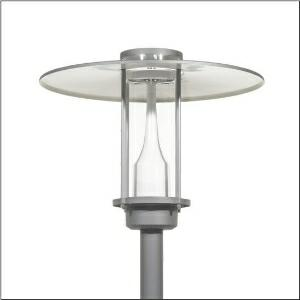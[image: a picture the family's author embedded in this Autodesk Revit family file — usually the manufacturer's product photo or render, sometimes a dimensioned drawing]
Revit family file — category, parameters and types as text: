
# Revit family: city-light_plus_iq___p1_0a_5xa5275bf14hp_a9e6
name_source: partatom
category: Lighting Fixtures
units: mm (PartAtom-declared; Revit-internal decimal feet)

## family parameters
Cut with Voids When Loaded = No
Host = Face
Light Source = No
Part Type = Normal
Room Calculation Point = No
Round Connector Dimension = Use Diameter
Shared = No

## types (1)
- --- (1 x LED, 3710 lm, 33.6 W, 2200K)
    Apparent Load = 34 VA
    CIE Flux Codes = 30 60 90 96 100
    Color Rendering = 70
    Color Temperature = 2200K
    Default Elevation = 1800 mm
    Description = City-Light Plus iQ, mast luminaire, Module 540 iQ-SR, primary light control with 3 zone facetted reflector, of plastic, silver coated, highly specular, structured, primary optical cover: cover, of PMMA, transparent, light distribution: P1.0a, light emission: direct distribution, primary light characteristic: strongly asymmetric, installation type: post-top, LED, High Power LED, rated luminous flux: 3.710lm, luminous efficacy: 110lm/W, light colour: 722, colour temperature: 2200K, control gear: iQ Street-Remote, control: pre-setting: logarithmic dimming characteristic, Street-Remote, Auto-Match, Temp-Guard, Lumen-Switch, Night-Set, Smart-Wire, Light-Fading, Desk-Remote (wireless, voltage-free reading and setting of iQ features in the workshop via application-optimized NFC function/RFID function), optimised constant luminous flux control (CLO 2.0), with terminal, 6-pole, max. 2.5mm², mains connection: 230..240V, AC, 50/60Hz, start of lifetime: 34W, end of service life: 36W, reduction: 15W, luminaire housing, upper part, of glass-fibre reinforced polyester, coated, Siteco® metallic grey (DB 702S), diameter: 750mm, height: 590mm, spigot size: d x l = 76 x 70mm (post-top) | with reducer (optional accessory) 60 x 70mm, mounting height: 3..5m, post-top mast mounting element, of diecast aluminium, coated, Siteco® metallic grey (DB 702S), Module 540 iQ-SR, traffic white (RAL 9016), equipment: Power, protection rating (complete): IP65, insulation class (complete): insulation class II (safety insulation), certification: CE, ENEC, VDE, packaging unit: 1 piece

Light Distribution: P1.0a
    Height = 590 mm
    Lamp = 1 x LED
    Lamp Light Flux = 3710 lm
    Lamp Power = 33.6 W
    Lamp count = 1
    Length = 750 mm
    Luminous efficacy = 110 lm/W
    Manufacturer = Siteco
    ModVariant = No
    Model = 5XA5275BF14HP
    Number of Poles = 1
    OnlyDefault = Yes
    Power Factor = 1
    Product Name = City-Light Plus iQ | P1.0a
    Product group = mast luminaire | pylon top
    ProductGroupID = 6100
    Protection Class = Protection class II
    Protection Degree = IP 65
    RLX_Detail_Level = 1
    RLX_Emergency_Light_Flux = 0 lm
    RLX_Emergency_Type = 0
    RLX_Emergency_Type_DB = No
    RlxData = <blob elided: 35065 chars, md5=6ac11954>
    Socket = socket
    Standby Power = 0 W
    System Light Flux = 3710 lm
    System Power = 34 W
    Type Comments = factory setting: luminous flux: 100 % | dim-lin: 254 | 695 mA
    Type Image = l_1006456.jpg
    URL = http://relux.com
    VarID = @adj_193772
    Voltage = 0 V
    Weight = 0.00 kg
    Width = 0 mm  [stored 0 ft]

note: [stored X ft] marks values corroborated as IEEE doubles in the binary element streams (Revit-internal decimal feet)

## geometry (parser evidence)
native form markers: Blend x4, Sweep x11
no freeform markers — native parametric forms only
